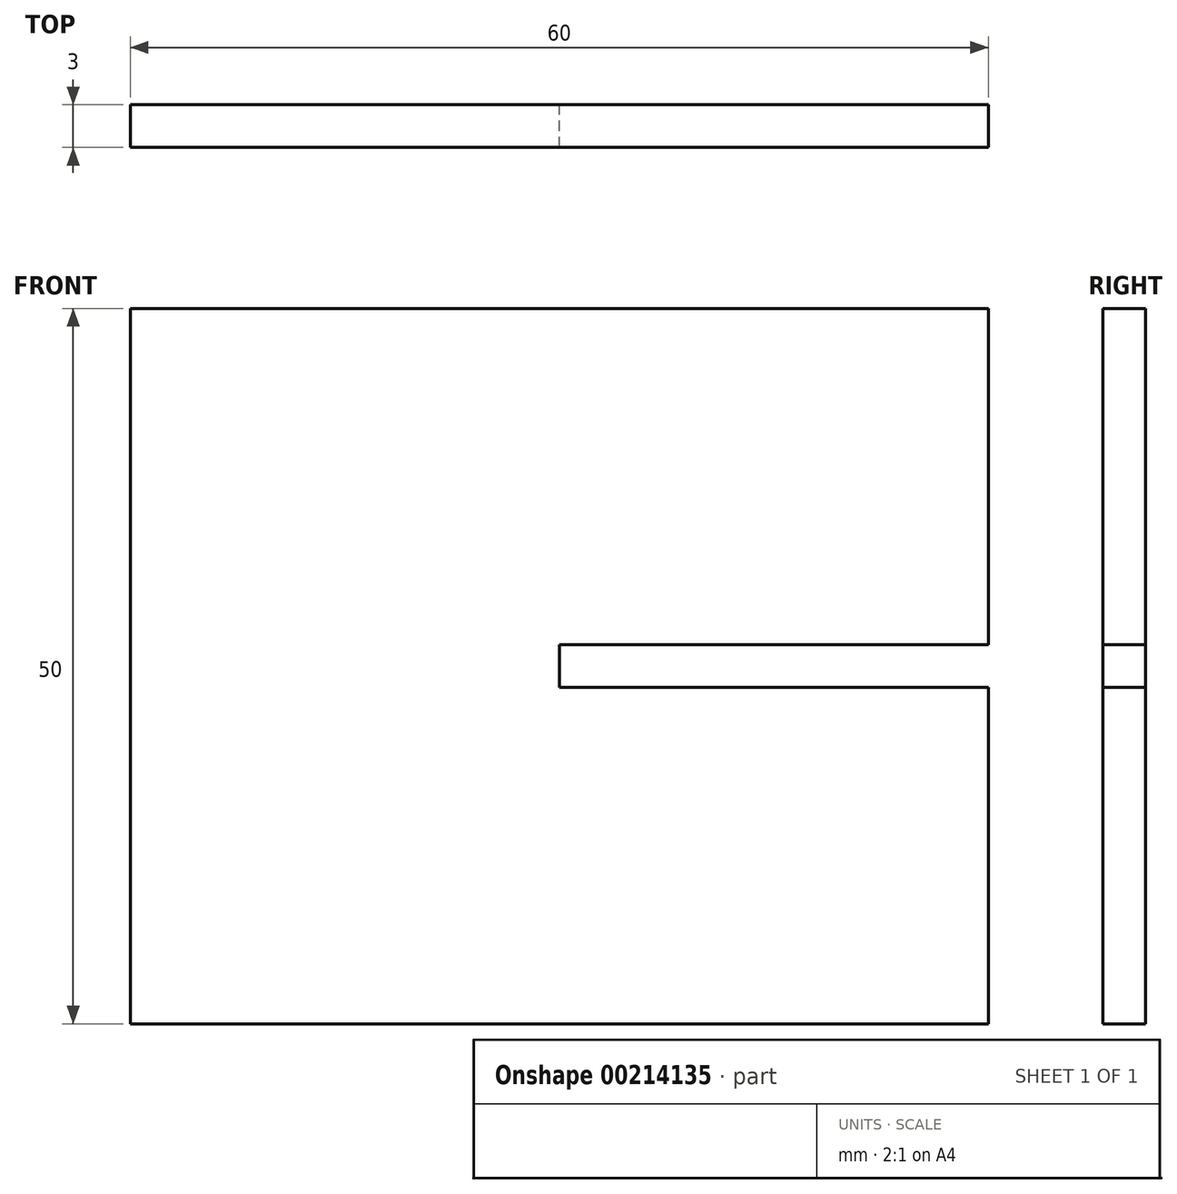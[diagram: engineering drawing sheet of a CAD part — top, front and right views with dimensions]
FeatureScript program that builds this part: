
annotation { "Feature Type Name" : "Feature", "Feature Type Description" : "" }
export const myFeature = defineFeature(function(context is Context, id is Id, definition is map)
    precondition{}
    {
        {
            var Q0;
            Q0=qCreatedBy(makeId("Front.planeOp"),FACE);
            var sketch = newSketch(context, id + "F0", { "sketchPlane" : qUnion([Q0])});
            skLineSegment(sketch, "E0.bottom", {"start": v(-30, 25) * mm, "end": v(30, 25) * mm});
            skLineSegment(sketch, "E0.top", {"start": v(-30, -25) * mm, "end": v(30, -25) * mm});
            skLineSegment(sketch, "E0.left", {"start": v(-30, 25) * mm, "end": v(-30, -25) * mm});
            skLineSegment(sketch, "E0.right", {"start": v(30, 25) * mm, "end": v(30, -25) * mm});
            skPoint(sketch, "E0.middle", {"position": v(0, 0) * mm});
            skPoint(sketch, "E1.oppositeSnap0", {"position": v(0, 25) * mm});
            skLineSegment(sketch, "E1.bottom", {"start": v(30, -1.5) * mm, "end": v(0, -1.5) * mm});
            skLineSegment(sketch, "E1.top", {"start": v(30, 1.5) * mm, "end": v(0, 1.5) * mm});
            skLineSegment(sketch, "E1.left", {"start": v(30, -1.5) * mm, "end": v(30, 1.5) * mm});
            skLineSegment(sketch, "E1.right", {"start": v(0, -1.5) * mm, "end": v(0, 1.5) * mm});
            skSolve(sketch);
        }
        {
            var Q0;
            {var subQ1=sQuery(id+"F0.wireOp",EDGE,"E0.bottom");Q0=makeQuery(id+"F0.imprint","IMPRINT",FACE,{"disambiguationData":[TD([[makeQuery(id+"F0.imprint","IMPRINT",EDGE,{"derivedFrom":subQ1}),-1.0]])]});}
            extrude(context, id + "F1", {"entities" : qUnion([Q0]), "depth" : 3 * mm});
        }
    });
